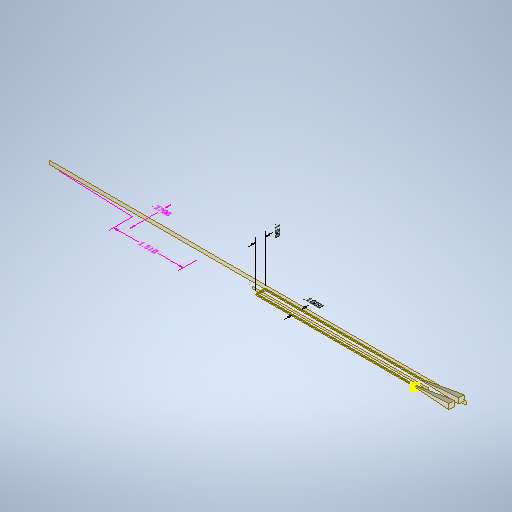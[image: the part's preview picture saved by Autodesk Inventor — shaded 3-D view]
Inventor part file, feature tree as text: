
AUTODESK INVENTOR PART (.ipt)
format: ipt  version: 2025.2 (Build 292293000, 293)  size: 308,224 bytes
history: native  units: in
note: dims shown in document units (in); Inventor stores cm internally (conversion verified against a paired STEP export)
features: other x6, plane x4, sketch x4, sweep x1, loft x1, mirror x1, projected_geometry x1
ambient origin geometry x8: Origin, YZ Plane, XZ Plane, XY Plane, X Axis, Y Axis, Z Axis, Center Point
bodies: Solid1 (feature_tree)
feature tree (18):
  other  "Annotations"
  sweep  "Sweep1"
  plane  "Work Plane1"
  plane  "Work Plane2"
  plane  "Work Plane4"
  sketch  "Sketch15"  dims[d86=-0.1175in]
  sketch  "Sketch16"  dims[d89=0.1in d90=0.0in d91=0.0in d92=0.0in d98=0.01in d99=0.01in d100=0.055in d102=0.055in d104=0.0in d109=0.0in d110=90.0deg d111=0.0in d112=90.0deg d116=-0.05in d113=0.0in d114=0.3937in d115=0.1in d117=0.086in d118=0.3123in d119=0.1in d42=0.2341in d43=0.169in d44=0.37in d48=0.2141in d49=0.2512in d50=1.51in]
  loft  "Loft3"
  plane  "Work Plane5"
  mirror  "Mirror3"
  sketch  "Sketch1"  dims[d6=0.0in d7=0.0in d11=0.375in d19=-0.25in]
  sketch  "Sketch2"  dims[d69=1.625in d70=1.625in]
  projected_geometry  "Projected Loop1"
  other  "Edges4"
  other  "Linear Dimension 1"
  other  "Linear Dimension 3"
  other  "Linear Dimension 4"
  other  "Linear Dimension 5"
